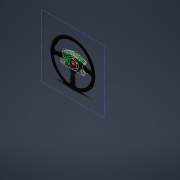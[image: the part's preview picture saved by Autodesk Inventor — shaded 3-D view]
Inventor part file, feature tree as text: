
AUTODESK INVENTOR PART (.ipt)
format: ipt  version: 2022 (Build 260153000, 153)  size: 2,673,152 bytes
history: native  units: mm
features: extrude x18, sketch x12, fillet x9, projected_geometry x6, other x3, chamfer x2, split x1, mirror x1, plane x1
ambient origin geometry x8: Origin, YZ Plane, XZ Plane, XY Plane, X Axis, Y Axis, Z Axis, Center Point
bodies: Solid1 (feature_tree)
feature tree (53):
  sketch  "Sketch1"  dims[d5=61.0mm d6=70.0mm]
  extrude  "Extrusion1"  Depth=70.0mm
  extrude  "Extrusion2"  Depth=60.0mm TaperAngle=360.0deg
  split  "Split1"
  sketch  "Sketch4"  dims[d14=86.0mm d36=20.0mm d37=0.0mm]
  sketch  "Sketch5"  dims[d38=40.0mm d49=75.888542mm]
  extrude  "Extrusion3"  Depth=20.0mm TaperAngle=0.0deg
  extrude  "Extrusion4"  Depth=75.888542mm
  extrude  "Extrusion5"  Depth=20.383104mm
  extrude  "Extrusion6"  Depth=28.0mm
  extrude  "Extrusion8"  Depth=1.5mm
  extrude  "Extrusion20"  Depth=50.0mm TaperAngle=360.0deg
  sketch  "Sketch7"  dims[d50=75.888542mm d51=20.383104mm]
  extrude  "Extrusion9"  Depth=10.0mm TaperAngle=360.0deg
  extrude  "Extrusion10"  Depth=13.5mm TaperAngle=0.0deg
  mirror  "Mirror1"
  extrude  "Extrusion11"  Depth=5.0mm
  extrude  "Extrusion12"  Depth=2.0mm TaperAngle=360.0deg
  chamfer  "Chamfer3"  Distance=13.5mm
  fillet  "Fillet1"  [1 undecoded]
  plane  "Work Plane4"
  sketch  "Sketch11"  dims[d54=1.5mm d55=0.0mm d61=10.458mm]
  sketch  "Sketch12"  dims[d62=9.0mm d63=50.0mm d65=360.0deg]
  extrude  "Extrusion14"  Depth=2.0mm
  extrude  "Extrusion19"  Depth=2.0mm
  extrude  "Extrusion15"  Depth=2.0mm
  fillet  "Fillet2"  [1 undecoded]
  fillet  "Fillet3"  Radius=2.0mm
  extrude  "Extrusion16"  Depth=2.0mm TaperAngle=0.0deg
  sketch  "Sketch15"  dims[d77=5.0mm d78=0.0mm d82=5.0mm]
  extrude  "Extrusion17"  Depth=2.0mm TaperAngle=0.0deg
  extrude  "Extrusion18"  Depth=2.0mm
  fillet  "Fillet4"  Radius=5.0mm
  fillet  "Fillet5"  Radius=3.5mm
  fillet  "Fillet6"  Radius=20.0mm
  fillet  "Fillet7"  Radius=20.0mm
  fillet  "Fillet9"  Radius=5.0mm
  chamfer  "Chamfer6"  Distance=5.0mm
  sketch  "Sketch17"  dims[d83=1.0mm d84=50.0mm d86=360.0deg d88=13.5mm d89=0.0mm d92=0.0mm d93=0.0mm d94=23.0mm d95=7.0mm d96=5.0mm d97=90.0deg d101=2.0mm d103=8.0mm d104=0.0mm d105=3.0mm d106=0.0mm d107=5.0mm d108=5.0mm d109=3.5mm d110=0.0mm d116=20.0mm d119=20.0mm d120=5.0mm d121=5.0mm d129=80.0mm d131=3.51199mm d148=2.0mm d149=0.0mm d154=1.5mm d155=2.0mm d156=45.0deg d164=7.0mm d165=1.0mm d166=50.0mm d168=360.0deg d170=0.0mm d242=1.0mm d243=1.0mm d244=1.0mm d245=1.0mm d246=1.0mm d247=1.0mm d248=1.0mm d249=1.0mm d250=1.0mm d251=1.0mm d252=1.0mm d253=1.0mm d254=1.0mm d255=1.0mm d256=1.0mm d257=1.0mm d258=1.0mm d259=1.0mm d260=1.0mm d261=1.0mm d262=1.0mm d263=1.0mm d264=1.0mm d265=1.0mm d266=1.0mm d267=1.0mm d268=1.0mm d269=1.0mm d270=1.0mm d271=1.0mm d272=1.0mm d273=1.0mm d274=1.0mm d275=1.0mm d276=1.0mm d277=1.0mm d278=1.0mm d279=1.0mm d280=1.0mm d281=1.0mm d282=1.0mm d283=1.0mm d284=1.0mm d285=1.0mm d286=1.0mm d287=1.0mm d288=1.0mm d289=1.0mm d290=1.0mm d291=1.0mm d292=1.0mm d293=1.0mm d294=1.0mm d295=1.0mm d296=1.0mm d297=1.0mm d298=1.0mm d299=1.0mm d300=1.0mm d301=1.0mm d302=1.0mm d303=1.0mm d304=1.0mm d305=1.0mm d306=1.0mm d307=1.0mm d308=1.0mm d309=1.0mm d310=1.0mm d311=1.0mm d312=1.0mm d313=1.0mm d314=1.0mm d315=1.0mm d316=1.0mm d317=1.0mm d318=1.0mm d319=1.0mm d320=1.0mm d321=1.0mm d322=1.0mm d323=1.0mm d324=1.0mm d325=1.0mm d326=1.0mm d327=1.0mm d328=1.0mm d329=1.0mm d330=1.0mm d331=1.0mm d332=1.0mm d333=1.0mm d334=1.0mm d335=1.0mm d336=1.0mm d337=1.0mm d338=1.0mm d339=1.0mm d340=1.0mm d341=1.0mm d342=1.0mm d343=1.0mm d344=1.0mm d345=1.0mm d348=10.5mm d349=0.0mm d350=5.0mm d351=8.061767mm d373=8.5mm d374=0.0mm d375=4.0mm d376=3.0mm d377=3.0mm d378=3.0mm d379=3.0mm d380=3.0mm d381=4.0mm d382=5.0mm d383=2.0mm d386=8.5mm d387=7.0mm d388=0.0mm d392=1.5mm d393=1.5mm d394=1.5mm d395=1.5mm d396=1.5mm d397=1.5mm d398=1.5mm d399=2.5mm d400=2.5mm d402=4.0mm d403=4.0mm d405=1.0mm d409=90.0deg d410=2.0mm d411=0.0mm d412=4.0mm d413=0.0mm d414=5.8mm d415=0.0mm d417=5.2mm d419=50.0mm d421=50.0mm d423=50.0mm d425=50.0mm d426=5.2mm d428=50.0mm d430=50.0mm d432=50.0mm d434=50.0mm d435=5.2mm d437=50.0mm d439=50.0mm d441=50.0mm d443=50.0mm d444=5.2mm d446=50.0mm d448=50.0mm d450=50.0mm d452=50.0mm d453=5.2mm d454=5.6mm d455=0.0mm d456=1.0mm d457=1.0mm d458=1.0mm d459=1.0mm d461=1.5mm d495=10.0mm d496=4.0mm d497=45.0deg d498=2.0mm d503=36.0mm d150=0.5mm d151=0.872665mm d152=0.5mm d153=0.872665mm d460=0.5mm d462=0.5mm d463=0.872665mm]
  fillet  "Fillet11"  Radius=80.0mm
  other  "Image1"
  other  "Image2"
  sketch  "Sketch2"  dims[d7=6.5mm d9=60.0mm d11=360.0deg]
  sketch  "Sketch8"  dims[d52=20.383104mm d53=28.0mm]
  sketch  "Sketch13"  dims[d67=10.0mm d68=50.0mm d70=360.0deg]
  sketch  "Sketch14"  dims[d72=0.0mm d73=0.0mm d74=13.5mm d75=0.0mm]
  projected_geometry  "Projected Loop4"
  projected_geometry  "Projected Loop5"
  projected_geometry  "Projected Loop6"
  projected_geometry  "Projected Loop7"
  projected_geometry  "Projected Loop8"
  projected_geometry  "Projected Loop9"
  other  "Image5"
note: 2 required parameter values undecoded (feature->parameter linkage not recoverable at this tier; creation-order binding heuristic only, values carry confidence <= 0.55)
